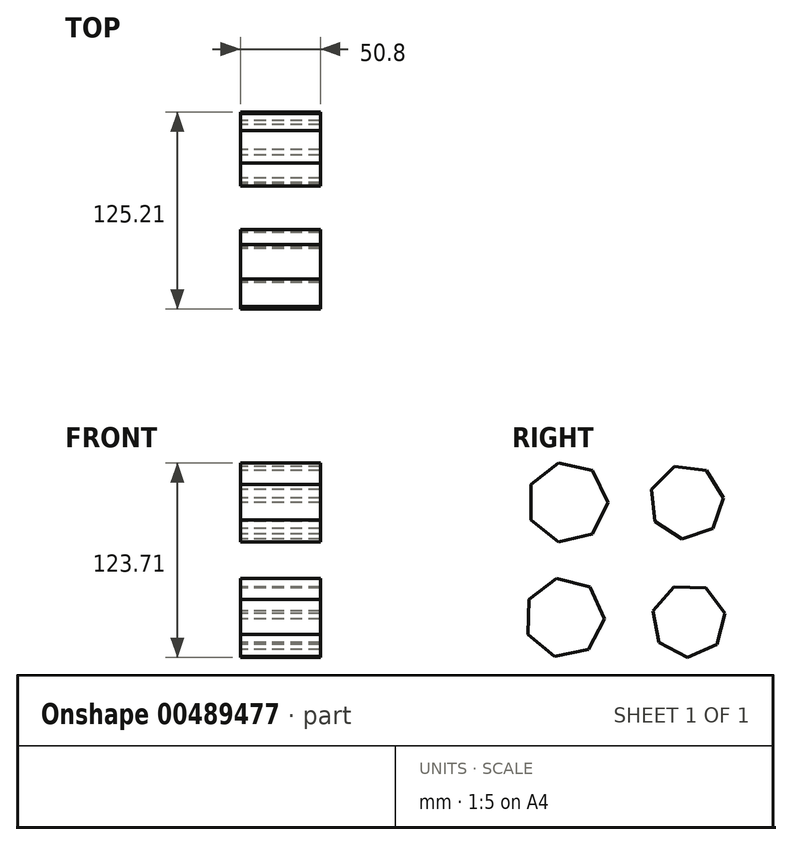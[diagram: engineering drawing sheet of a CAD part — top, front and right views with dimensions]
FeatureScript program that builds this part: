
annotation { "Feature Type Name" : "Feature", "Feature Type Description" : "" }
export const myFeature = defineFeature(function(context is Context, id is Id, definition is map)
    precondition{}
    {
        {
            var Q0;
            Q0=qCreatedBy(makeId("Right.planeOp"),FACE);
            var sketch = newSketch(context, id + "F0", { "sketchPlane" : qUnion([Q0])});
            skPoint(sketch, "E0.orphan", {"position": v(0, 0) * mm});
            skPoint(sketch, "E1.end.orphan", {"position": v(0, 75.93) * mm});
            skPoint(sketch, "E1.start.orphan", {"position": v(-76.32, 0) * mm});
            skCircle(sketch, "E2.cCircle", {"center": v(-36.57, 33.38) * mm, "radius": 23.19 * mm, "construction": true});
            skLineSegment(sketch, "E2.0", {"start": v(-59.75, 22.21) * mm, "end": v(-59.75, 44.55) * mm});
            skLineSegment(sketch, "E2.1", {"start": v(-59.75, 44.55) * mm, "end": v(-42.3, 58.47) * mm});
            skLineSegment(sketch, "E2.2", {"start": v(-42.3, 58.47) * mm, "end": v(-20.52, 53.5) * mm});
            skLineSegment(sketch, "E2.3", {"start": v(-20.52, 53.5) * mm, "end": v(-10.83, 33.38) * mm});
            skLineSegment(sketch, "E2.4", {"start": v(-10.83, 33.38) * mm, "end": v(-20.52, 13.26) * mm});
            skLineSegment(sketch, "E2.5", {"start": v(-20.52, 13.26) * mm, "end": v(-42.3, 8.29) * mm});
            skLineSegment(sketch, "E2.6", {"start": v(-42.3, 8.29) * mm, "end": v(-59.75, 22.21) * mm});
            skPoint(sketch, "E2.0.midPoint", {"position": v(-59.75, 33.38) * mm});
            skCircle(sketch, "E3.cCircle", {"center": v(39.11, 33.63) * mm, "radius": 21.36 * mm, "construction": true});
            skLineSegment(sketch, "E3.0", {"start": v(62.68, 36.2) * mm, "end": v(55.8, 16.8) * mm});
            skLineSegment(sketch, "E3.1", {"start": v(55.8, 16.8) * mm, "end": v(36.36, 10.1) * mm});
            skLineSegment(sketch, "E3.2", {"start": v(36.36, 10.1) * mm, "end": v(19, 21.1) * mm});
            skLineSegment(sketch, "E3.3", {"start": v(19, 21.1) * mm, "end": v(16.77, 41.55) * mm});
            skLineSegment(sketch, "E3.4", {"start": v(16.77, 41.55) * mm, "end": v(31.37, 56.04) * mm});
            skLineSegment(sketch, "E3.5", {"start": v(31.37, 56.04) * mm, "end": v(51.8, 53.66) * mm});
            skLineSegment(sketch, "E3.6", {"start": v(51.8, 53.66) * mm, "end": v(62.68, 36.2) * mm});
            skPoint(sketch, "E3.0.midPoint", {"position": v(59.24, 26.5) * mm});
            skCircle(sketch, "E4.cCircle", {"center": v(-38.35, -40) * mm, "radius": 22.9 * mm, "construction": true});
            skLineSegment(sketch, "E4.0", {"start": v(-12.93, -40.64) * mm, "end": v(-23, -60.27) * mm});
            skLineSegment(sketch, "E4.1", {"start": v(-23, -60.27) * mm, "end": v(-44.62, -64.64) * mm});
            skLineSegment(sketch, "E4.2", {"start": v(-44.62, -64.64) * mm, "end": v(-61.52, -50.46) * mm});
            skLineSegment(sketch, "E4.3", {"start": v(-61.52, -50.46) * mm, "end": v(-60.97, -28.4) * mm});
            skLineSegment(sketch, "E4.4", {"start": v(-60.97, -28.4) * mm, "end": v(-43.39, -15.09) * mm});
            skLineSegment(sketch, "E4.5", {"start": v(-43.39, -15.09) * mm, "end": v(-22, -20.53) * mm});
            skLineSegment(sketch, "E4.6", {"start": v(-22, -20.53) * mm, "end": v(-12.93, -40.64) * mm});
            skPoint(sketch, "E4.0.midPoint", {"position": v(-17.96, -50.45) * mm});
            skCircle(sketch, "E5.cCircle", {"center": v(40.64, -41.79) * mm, "radius": 21.14 * mm, "construction": true});
            skLineSegment(sketch, "E5.0", {"start": v(17.96, -35.76) * mm, "end": v(31.22, -20.3) * mm});
            skLineSegment(sketch, "E5.1", {"start": v(31.22, -20.3) * mm, "end": v(51.57, -21.02) * mm});
            skLineSegment(sketch, "E5.2", {"start": v(51.57, -21.02) * mm, "end": v(63.7, -37.38) * mm});
            skLineSegment(sketch, "E5.3", {"start": v(63.7, -37.38) * mm, "end": v(58.46, -57.06) * mm});
            skLineSegment(sketch, "E5.4", {"start": v(58.46, -57.06) * mm, "end": v(39.81, -65.24) * mm});
            skLineSegment(sketch, "E5.5", {"start": v(39.81, -65.24) * mm, "end": v(21.79, -55.76) * mm});
            skLineSegment(sketch, "E5.6", {"start": v(21.79, -55.76) * mm, "end": v(17.96, -35.76) * mm});
            skPoint(sketch, "E5.0.midPoint", {"position": v(24.59, -28.03) * mm});
            skSolve(sketch);
        }
        {
            var Q0;
            Q0=makeQuery(id+"F0.imprint","IMPRINT",FACE,{"disambiguationData":[TD([[makeQuery(id+"F0.imprint","IMPRINT",EDGE,{"derivedFrom":sQuery(id+"F0.wireOp",EDGE,"E5.0")}),-1.0]])]});
            var sketch = newSketch(context, id + "F1", { "sketchPlane" : qUnion([Q0])});
            skSolve(sketch);
        }
        {
            var Q0;
            Q0 = qSketchRegion(id + "F1", true);
            var Q1;
            Q1=makeQuery(id+"F0.imprint","IMPRINT",FACE,{"disambiguationData":[TD([[makeQuery(id+"F0.imprint","IMPRINT",EDGE,{"derivedFrom":sQuery(id+"F0.wireOp",EDGE,"E2.0")}),-1.0]])]});
            var Q2;
            Q2=makeQuery(id+"F0.imprint","IMPRINT",FACE,{"disambiguationData":[TD([[makeQuery(id+"F0.imprint","IMPRINT",EDGE,{"derivedFrom":sQuery(id+"F0.wireOp",EDGE,"E4.0")}),-1.0]])]});
            var Q3;
            Q3=makeQuery(id+"F0.imprint","IMPRINT",FACE,{"disambiguationData":[TD([[makeQuery(id+"F0.imprint","IMPRINT",EDGE,{"derivedFrom":sQuery(id+"F0.wireOp",EDGE,"E5.0")}),-1.0]])]});
            var Q4;
            Q4=makeQuery(id+"F0.imprint","IMPRINT",FACE,{"disambiguationData":[TD([[makeQuery(id+"F0.imprint","IMPRINT",EDGE,{"derivedFrom":sQuery(id+"F0.wireOp",EDGE,"E3.0")}),-1.0]])]});
            extrude(context, id + "F2", {"entities" : qUnion([Q0, Q1, Q2, Q3, Q4]), "depth" : 50.8 * mm});
        }
    });
